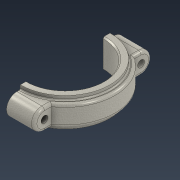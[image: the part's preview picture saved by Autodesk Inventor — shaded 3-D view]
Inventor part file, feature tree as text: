
AUTODESK INVENTOR PART (.ipt)
format: ipt  version: 2022 (Build 260153000, 153)  size: 184,320 bytes
history: native  units: mm
features: sketch x2, extrude x2, other x2, fillet x2, hole x1, chamfer x1
ambient origin geometry x8: Origin, YZ Plane, XZ Plane, XY Plane, X Axis, Y Axis, Z Axis, Center Point
bodies: Solid1 (feature_tree)
feature tree (10):
  sketch  "Sketch1"  dims[d0=27.5mm d1=32.5mm]
  extrude  "Extrusion1"  Depth=32.5mm
  extrude  "Extrusion2"  Depth=1.0mm
  hole  "Hole1"  [1 undecoded]
  other  "Full Round Fillet1"
  other  "Full Round Fillet2"
  fillet  "Fillet1"  Radius=21.0mm
  chamfer  "Chamfer1"  Distance=15.0mm
  fillet  "Fillet2"  Radius=7.5mm
  sketch  "Sketch2"  dims[d2=10.0mm d3=20.0mm d4=36.0mm d5=21.0mm d6=0.0mm d7=15.0mm d8=0.0mm d9=7.5mm d10=7.5mm d11=5.0mm d12=6.0mm d13=4.0mm d14=2.0mm d15=90.0deg d16=8.0mm d17=20.594885mm d18=2.0mm d19=1.0mm d20=2.0mm d21=45.0deg d22=1.0mm]
note: 1 required parameter value undecoded (feature->parameter linkage not recoverable at this tier; creation-order binding heuristic only, values carry confidence <= 0.55)
